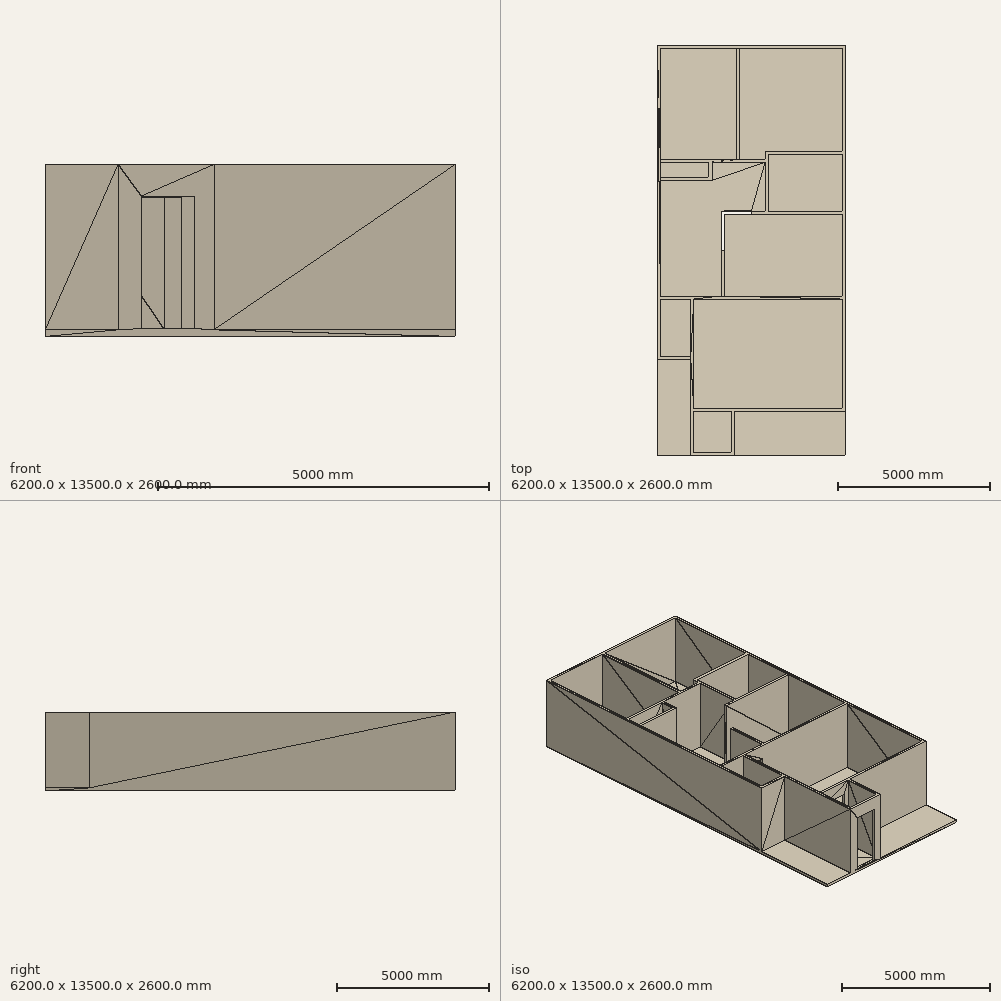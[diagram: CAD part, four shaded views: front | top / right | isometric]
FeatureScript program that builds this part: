
annotation { "Feature Type Name" : "Feature", "Feature Type Description" : "" }
export const myFeature = defineFeature(function(context is Context, id is Id, definition is map)
    precondition{}
    {
        {
            var Q0;
            Q0=qCreatedBy(makeId("Top.planeOp"),FACE);
            var sketch = newSketch(context, id + "F0", { "sketchPlane" : qUnion([Q0])});
            skLineSegment(sketch, "E0.bottom", {"start": v(-3100, -6750) * mm, "end": v(3100, -6750) * mm});
            skLineSegment(sketch, "E0.top", {"start": v(-3100, 6750) * mm, "end": v(3100, 6750) * mm});
            skLineSegment(sketch, "E0.left", {"start": v(-3100, -6750) * mm, "end": v(-3100, 6750) * mm});
            skLineSegment(sketch, "E0.right", {"start": v(3100, -6750) * mm, "end": v(3100, 6750) * mm});
            skPoint(sketch, "E0.middle", {"position": v(0, 0) * mm});
            skSolve(sketch);
        }
        {
            var Q0;
            Q0=qSketchRegion(id+"F0",true);
            extrude(context, id + "F1", {"entities" : qUnion([Q0]), "depth" : 100 * mm});
        }
        {
            var Q0;
            Q0=makeQuery(id+"F1.opExtrude","CAP_FACE",FACE,{"disambiguationData":[OSD([sQuery(id+"F0.wireOp",EDGE,"E0.bottom"),sQuery(id+"F0.wireOp",EDGE,"E0.top"),sQuery(id+"F0.wireOp",EDGE,"E0.left"),sQuery(id+"F0.wireOp",EDGE,"E0.right")])],"isStart":false});
            var sketch = newSketch(context, id + "F2", { "sketchPlane" : qUnion([Q0])});
            skLineSegment(sketch, "E1", {"start": v(-3100, 6750) * mm, "end": v(-3100, -3600) * mm});
            skLineSegment(sketch, "E2", {"start": v(-3100, -3600) * mm, "end": v(-2000, -3600) * mm});
            skLineSegment(sketch, "E3", {"start": v(-2000, -3600) * mm, "end": v(-2000, -6750) * mm});
            skLineSegment(sketch, "E4", {"start": v(-2000, -6750) * mm, "end": v(-550, -6750) * mm});
            skLineSegment(sketch, "E5", {"start": v(-550, -6750) * mm, "end": v(-550, -5300) * mm});
            skLineSegment(sketch, "E6", {"start": v(-550, -5300) * mm, "end": v(3100, -5300) * mm});
            skLineSegment(sketch, "E7", {"start": v(3100, -5300) * mm, "end": v(3100, 6750) * mm});
            skLineSegment(sketch, "E8", {"start": v(3100, 6750) * mm, "end": v(-3100, 6750) * mm});
            skLineSegment(sketch, "E9.0", {"start": v(3000, 6650) * mm, "end": v(-3000, 6650) * mm});
            skLineSegment(sketch, "E9.1", {"start": v(3000, -5200) * mm, "end": v(3000, 6650) * mm});
            skLineSegment(sketch, "E9.2", {"start": v(-3000, 6650) * mm, "end": v(-3000, -3500) * mm});
            skLineSegment(sketch, "E9.3", {"start": v(-650, -5200) * mm, "end": v(3000, -5200) * mm});
            skLineSegment(sketch, "E9.4", {"start": v(-3000, -3500) * mm, "end": v(-1900, -3500) * mm});
            skLineSegment(sketch, "E9.5", {"start": v(-1900, -3500) * mm, "end": v(-1900, -6650) * mm});
            skLineSegment(sketch, "E9.6", {"start": v(-1900, -6650) * mm, "end": v(-650, -6650) * mm});
            skLineSegment(sketch, "E9.7", {"start": v(-650, -6650) * mm, "end": v(-650, -5200) * mm});
            skSolve(sketch);
        }
        {
            var Q0;
            Q0=qSketchRegion(id+"F2",true);
            extrude(context, id + "F3", {"entities" : qUnion([Q0]), "operationType" : NewBodyOperationType.ADD, "depth" : 2500 * mm});
        }
        {
            var Q0;
            Q0=makeQuery(id+"F3.boolean.opBoolean","SPLIT",FACE,{"disambiguationData":[TD([makeQuery(id+"F3.opExtrude","SWEPT_FACE",FACE,{"disambiguationData":[OSD([sQuery(id+"F2.wireOp",EDGE,"E9.0")])]})])],"derivedFrom":makeQuery(id+"F1.opExtrude","CAP_FACE",FACE,{"disambiguationData":[OSD([sQuery(id+"F0.wireOp",EDGE,"E0.bottom"),sQuery(id+"F0.wireOp",EDGE,"E0.top"),sQuery(id+"F0.wireOp",EDGE,"E0.left"),sQuery(id+"F0.wireOp",EDGE,"E0.right")])],"isStart":false})});
            var sketch = newSketch(context, id + "F4", { "sketchPlane" : qUnion([Q0])});
            skLineSegment(sketch, "E10", {"start": v(-650, -5300) * mm, "end": v(-1900, -5300) * mm});
            skLineSegment(sketch, "E11", {"start": v(-1900, -5300) * mm, "end": v(-1900, -5200) * mm});
            skLineSegment(sketch, "E12", {"start": v(-1900, -5200) * mm, "end": v(-650, -5200) * mm});
            skLineSegment(sketch, "E13", {"start": v(-650, -5200) * mm, "end": v(-650, -5300) * mm});
            skSolve(sketch);
        }
        {
            var Q0;
            Q0=qSketchRegion(id+"F4",true);
            extrude(context, id + "F5", {"entities" : qUnion([Q0]), "operationType" : NewBodyOperationType.ADD, "depth" : 2500 * mm});
        }
        {
            var Q0;
            {var subQ3=makeQuery(id+"F3.opExtrude","SWEPT_FACE",FACE,{"disambiguationData":[OSD([sQuery(id+"F2.wireOp",EDGE,"E9.0")])]});Q0=makeQuery(id+"F5.boolean.opBoolean","SPLIT",FACE,{"disambiguationData":[TD([subQ3])],"derivedFrom":makeQuery(id+"F3.boolean.opBoolean","SPLIT",FACE,{"disambiguationData":[TD([subQ3])],"derivedFrom":makeQuery(id+"F1.opExtrude","CAP_FACE",FACE,{"disambiguationData":[OSD([sQuery(id+"F0.wireOp",EDGE,"E0.bottom"),sQuery(id+"F0.wireOp",EDGE,"E0.top"),sQuery(id+"F0.wireOp",EDGE,"E0.left"),sQuery(id+"F0.wireOp",EDGE,"E0.right")])],"isStart":false})})});}
            var sketch = newSketch(context, id + "F6", { "sketchPlane" : qUnion([Q0])});
            skLineSegment(sketch, "E14", {"start": v(-3000, -1600) * mm, "end": v(-3000, -1500) * mm});
            skLineSegment(sketch, "E15", {"start": v(-3000, -1500) * mm, "end": v(3000, -1500) * mm});
            skLineSegment(sketch, "E16", {"start": v(3000, -1500) * mm, "end": v(3000, -1600) * mm});
            skLineSegment(sketch, "E17", {"start": v(3000, -1600) * mm, "end": v(-3000, -1600) * mm});
            skSolve(sketch);
        }
        {
            var Q0;
            Q0=qSketchRegion(id+"F6",true);
            extrude(context, id + "F7", {"entities" : qUnion([Q0]), "operationType" : NewBodyOperationType.ADD, "depth" : 2500 * mm});
        }
        {
            var Q0;
            {var subQ1=makeQuery(id+"F3.opExtrude","SWEPT_FACE",FACE,{"disambiguationData":[OSD([sQuery(id+"F2.wireOp",EDGE,"E9.3")])]});var subQ6=makeQuery(id+"F3.opExtrude","SWEPT_FACE",FACE,{"disambiguationData":[OSD([sQuery(id+"F2.wireOp",EDGE,"E9.0")])]});Q0=makeQuery(id+"F7.boolean.opBoolean","SPLIT",FACE,{"disambiguationData":[TD([subQ1])],"derivedFrom":makeQuery(id+"F5.boolean.opBoolean","SPLIT",FACE,{"disambiguationData":[TD([subQ6])],"derivedFrom":makeQuery(id+"F3.boolean.opBoolean","SPLIT",FACE,{"disambiguationData":[TD([subQ6])],"derivedFrom":makeQuery(id+"F1.opExtrude","CAP_FACE",FACE,{"disambiguationData":[OSD([sQuery(id+"F0.wireOp",EDGE,"E0.bottom"),sQuery(id+"F0.wireOp",EDGE,"E0.top"),sQuery(id+"F0.wireOp",EDGE,"E0.left"),sQuery(id+"F0.wireOp",EDGE,"E0.right")])],"isStart":false})})})});}
            var sketch = newSketch(context, id + "F8", { "sketchPlane" : qUnion([Q0])});
            skLineSegment(sketch, "E18", {"start": v(-1900, -3500) * mm, "end": v(-1900, -1600) * mm});
            skLineSegment(sketch, "E19", {"start": v(-1900, -1600) * mm, "end": v(-2000, -1600) * mm});
            skLineSegment(sketch, "E20", {"start": v(-2000, -1600) * mm, "end": v(-2000, -3500) * mm});
            skLineSegment(sketch, "E21", {"start": v(-2000, -3500) * mm, "end": v(-1900, -3500) * mm});
            skSolve(sketch);
        }
        {
            var Q0;
            Q0=qSketchRegion(id+"F8",true);
            extrude(context, id + "F9", {"entities" : qUnion([Q0]), "operationType" : NewBodyOperationType.ADD, "depth" : 2500 * mm});
        }
        {
            var Q0;
            {var subQ0=makeQuery(id+"F3.opExtrude","SWEPT_FACE",FACE,{"disambiguationData":[OSD([sQuery(id+"F2.wireOp",EDGE,"E9.0")])]});Q0=makeQuery(id+"F7.boolean.opBoolean","SPLIT",FACE,{"disambiguationData":[TD([subQ0])],"derivedFrom":makeQuery(id+"F5.boolean.opBoolean","SPLIT",FACE,{"disambiguationData":[TD([subQ0])],"derivedFrom":makeQuery(id+"F3.boolean.opBoolean","SPLIT",FACE,{"disambiguationData":[TD([subQ0])],"derivedFrom":makeQuery(id+"F1.opExtrude","CAP_FACE",FACE,{"disambiguationData":[OSD([sQuery(id+"F0.wireOp",EDGE,"E0.bottom"),sQuery(id+"F0.wireOp",EDGE,"E0.top"),sQuery(id+"F0.wireOp",EDGE,"E0.left"),sQuery(id+"F0.wireOp",EDGE,"E0.right")])],"isStart":false})})})});}
            var sketch = newSketch(context, id + "F10", { "sketchPlane" : qUnion([Q0])});
            skLineSegment(sketch, "E22", {"start": v(-900, -1500) * mm, "end": v(-1000, -1500) * mm});
            skLineSegment(sketch, "E23", {"start": v(-1000, -1500) * mm, "end": v(-1000, 1300) * mm});
            skLineSegment(sketch, "E24", {"start": v(-1000, 1300) * mm, "end": v(450, 1300) * mm});
            skLineSegment(sketch, "E25", {"start": v(450, 1300) * mm, "end": v(450, 3250) * mm});
            skLineSegment(sketch, "E26", {"start": v(450, 3250) * mm, "end": v(3000, 3250) * mm});
            skLineSegment(sketch, "E27", {"start": v(3000, 3250) * mm, "end": v(3000, 3150) * mm});
            skLineSegment(sketch, "E28", {"start": v(3000, 3150) * mm, "end": v(550, 3150) * mm});
            skLineSegment(sketch, "E29", {"start": v(550, 3150) * mm, "end": v(550, 1300) * mm});
            skLineSegment(sketch, "E30", {"start": v(550, 1300) * mm, "end": v(3000, 1300) * mm});
            skLineSegment(sketch, "E31", {"start": v(3000, 1300) * mm, "end": v(3000, 1200) * mm});
            skLineSegment(sketch, "E32", {"start": v(3000, 1200) * mm, "end": v(-900, 1200) * mm});
            skLineSegment(sketch, "E33", {"start": v(-900, 1200) * mm, "end": v(-900, -1500) * mm});
            skSolve(sketch);
        }
        {
            var Q0;
            Q0=qSketchRegion(id+"F10",true);
            extrude(context, id + "F11", {"entities" : qUnion([Q0]), "operationType" : NewBodyOperationType.ADD, "depth" : 2500 * mm});
        }
        {
            var Q0;
            {var subQ3=makeQuery(id+"F3.opExtrude","SWEPT_FACE",FACE,{"disambiguationData":[OSD([sQuery(id+"F2.wireOp",EDGE,"E9.0")])]});Q0=makeQuery(id+"F11.boolean.opBoolean","SPLIT",FACE,{"disambiguationData":[TD([subQ3])],"derivedFrom":makeQuery(id+"F7.boolean.opBoolean","SPLIT",FACE,{"disambiguationData":[TD([subQ3])],"derivedFrom":makeQuery(id+"F5.boolean.opBoolean","SPLIT",FACE,{"disambiguationData":[TD([subQ3])],"derivedFrom":makeQuery(id+"F3.boolean.opBoolean","SPLIT",FACE,{"disambiguationData":[TD([subQ3])],"derivedFrom":makeQuery(id+"F1.opExtrude","CAP_FACE",FACE,{"disambiguationData":[OSD([sQuery(id+"F0.wireOp",EDGE,"E0.bottom"),sQuery(id+"F0.wireOp",EDGE,"E0.top"),sQuery(id+"F0.wireOp",EDGE,"E0.left"),sQuery(id+"F0.wireOp",EDGE,"E0.right")])],"isStart":false})})})})});}
            var sketch = newSketch(context, id + "F12", { "sketchPlane" : qUnion([Q0])});
            skLineSegment(sketch, "E34", {"start": v(450, 3000) * mm, "end": v(450, 2900) * mm});
            skLineSegment(sketch, "E35", {"start": v(450, 2900) * mm, "end": v(-1300, 2900) * mm});
            skLineSegment(sketch, "E36", {"start": v(-1300, 2900) * mm, "end": v(-1300, 2300) * mm});
            skLineSegment(sketch, "E37", {"start": v(-1300, 2300) * mm, "end": v(-3000, 2300) * mm});
            skLineSegment(sketch, "E38", {"start": v(-3000, 2300) * mm, "end": v(-3000, 2400) * mm});
            skLineSegment(sketch, "E39", {"start": v(-3000, 2400) * mm, "end": v(-1400, 2400) * mm});
            skLineSegment(sketch, "E40", {"start": v(-1400, 2400) * mm, "end": v(-1400, 2900) * mm});
            skLineSegment(sketch, "E41", {"start": v(-1400, 2900) * mm, "end": v(-3000, 2900) * mm});
            skLineSegment(sketch, "E42", {"start": v(-3000, 2900) * mm, "end": v(-3000, 3000) * mm});
            skLineSegment(sketch, "E43", {"start": v(-3000, 3000) * mm, "end": v(-500, 3000) * mm});
            skLineSegment(sketch, "E44", {"start": v(-500, 3000) * mm, "end": v(-500, 6650) * mm});
            skLineSegment(sketch, "E45", {"start": v(-500, 6650) * mm, "end": v(-400, 6650) * mm});
            skLineSegment(sketch, "E46", {"start": v(-400, 6650) * mm, "end": v(-400, 3000) * mm});
            skLineSegment(sketch, "E47", {"start": v(-400, 3000) * mm, "end": v(450, 3000) * mm});
            skSolve(sketch);
        }
        {
            var Q0;
            Q0=qSketchRegion(id+"F12",true);
            extrude(context, id + "F13", {"entities" : qUnion([Q0]), "operationType" : NewBodyOperationType.ADD, "depth" : 2500 * mm});
        }
        {
            var Q0;
            Q0=makeQuery(id+"F3.boolean.opBoolean","MERGE",FACE,{"derivedFrom":[makeQuery(id+"F1.opExtrude","SWEPT_FACE",FACE,{"disambiguationData":[OSD([sQuery(id+"F0.wireOp",EDGE,"E0.bottom")])]}),makeQuery(id+"F3.opExtrude","SWEPT_FACE",FACE,{"disambiguationData":[OSD([sQuery(id+"F2.wireOp",EDGE,"E4")])]})]});
            var sketch = newSketch(context, id + "F14", { "sketchPlane" : qUnion([Q0])});
            skLineSegment(sketch, "E48.bottom", {"start": v(-1650, 120) * mm, "end": v(-850, 120) * mm});
            skLineSegment(sketch, "E48.top", {"start": v(-1650, 2120) * mm, "end": v(-850, 2120) * mm});
            skLineSegment(sketch, "E48.left", {"start": v(-1650, 120) * mm, "end": v(-1650, 2120) * mm});
            skLineSegment(sketch, "E48.right", {"start": v(-850, 120) * mm, "end": v(-850, 2120) * mm});
            skSolve(sketch);
        }
        {
            var Q0;
            Q0=qSketchRegion(id+"F14",true);
            extrude(context, id + "F15", {"entities" : qUnion([Q0]), "operationType" : NewBodyOperationType.REMOVE, "endBound" : BoundingType.UP_TO_NEXT, "oppositeDirection" : true, "depth" : 25 * mm});
        }
        {
            var Q0;
            Q0=makeQuery(id+"F5.opExtrude","SWEPT_FACE",FACE,{"disambiguationData":[OSD([sQuery(id+"F4.wireOp",EDGE,"E10")])]});
            var sketch = newSketch(context, id + "F16", { "sketchPlane" : qUnion([Q0])});
            skLineSegment(sketch, "E49.bottom", {"start": v(-1650, 120) * mm, "end": v(-850, 120) * mm});
            skLineSegment(sketch, "E49.top", {"start": v(-1650, 2120) * mm, "end": v(-850, 2120) * mm});
            skLineSegment(sketch, "E49.left", {"start": v(-1650, 120) * mm, "end": v(-1650, 2120) * mm});
            skLineSegment(sketch, "E49.right", {"start": v(-850, 120) * mm, "end": v(-850, 2120) * mm});
            skSolve(sketch);
        }
        {
            var Q0;
            Q0=qSketchRegion(id+"F16",true);
            extrude(context, id + "F17", {"entities" : qUnion([Q0]), "operationType" : NewBodyOperationType.REMOVE, "endBound" : BoundingType.UP_TO_NEXT, "oppositeDirection" : true, "depth" : 25 * mm});
        }
        {
            var Q0;
            {var subQ2=sQuery(id+"F2.wireOp",EDGE,"E9.1");var subQ3=sQuery(id+"F6.wireOp",EDGE,"E17");Q0=makeQuery(id+"F9.boolean.opBoolean","SPLIT",FACE,{"disambiguationData":[TD([makeQuery(id+"F3.opExtrude","SWEPT_FACE",FACE,{"disambiguationData":[OSD([subQ2])]})])],"derivedFrom":makeQuery(id+"F7.opExtrude","SWEPT_FACE",FACE,{"disambiguationData":[OSD([subQ3])]})});}
            var sketch = newSketch(context, id + "F18", { "sketchPlane" : qUnion([Q0])});
            skLineSegment(sketch, "E50.bottom", {"start": v(-1850, 100) * mm, "end": v(-1050, 100) * mm});
            skLineSegment(sketch, "E50.top", {"start": v(-1850, 2100) * mm, "end": v(-1050, 2100) * mm});
            skLineSegment(sketch, "E50.left", {"start": v(-1850, 100) * mm, "end": v(-1850, 2100) * mm});
            skLineSegment(sketch, "E50.right", {"start": v(-1050, 100) * mm, "end": v(-1050, 2100) * mm});
            skSolve(sketch);
        }
        {
            var Q0;
            Q0=qSketchRegion(id+"F18",true);
            extrude(context, id + "F19", {"entities" : qUnion([Q0]), "operationType" : NewBodyOperationType.REMOVE, "endBound" : BoundingType.UP_TO_NEXT, "oppositeDirection" : true, "depth" : 25 * mm});
        }
        {
            var Q0;
            Q0=makeQuery(id+"F1.opExtrude","SWEPT_BODY",BODY,{"disambiguationData":[OSD([sQuery(id+"F0.wireOp",EDGE,"E0.bottom"),sQuery(id+"F0.wireOp",EDGE,"E0.top"),sQuery(id+"F0.wireOp",EDGE,"E0.left"),sQuery(id+"F0.wireOp",EDGE,"E0.right")])]});
            transform(context, id + "F20", {"entities" : qUnion([Q0]), "transformType" : TransformType.TRANSLATION_3D, "dx" : 0 * mm, "dy" : 0 * mm, "dz" : 0 * mm, "makeCopy" : true});
        }
        {
            var Q0;
            Q0=makeQuery(id+"F11.opExtrude","SWEPT_FACE",FACE,{"disambiguationData":[OSD([sQuery(id+"F10.wireOp",EDGE,"E32")])]});
            var sketch = newSketch(context, id + "F21", { "sketchPlane" : qUnion([Q0])});
            skLineSegment(sketch, "E51.bottom", {"start": v(-900, 2600) * mm, "end": v(0, 2600) * mm});
            skLineSegment(sketch, "E51.top", {"start": v(-900, 0) * mm, "end": v(0, 0) * mm});
            skLineSegment(sketch, "E51.left", {"start": v(-900, 2600) * mm, "end": v(-900, 0) * mm});
            skLineSegment(sketch, "E51.right", {"start": v(0, 2600) * mm, "end": v(0, 0) * mm});
            skSolve(sketch);
        }
        {
            var Q0;
            Q0 = qSketchRegion(id + "F21", true);
            extrude(context, id + "F22", {"entities" : qUnion([Q0]), "operationType" : NewBodyOperationType.REMOVE, "oppositeDirection" : true, "depth" : 101 * mm, "offsetDistance" : 25 * mm});
        }
        {
            var Q0;
            Q0=makeQuery(id+"F22.boolean.opBoolean","MERGE",FACE,{"derivedFrom":[makeQuery(id+"F11.opExtrude","SWEPT_FACE",FACE,{"disambiguationData":[OSD([sQuery(id+"F10.wireOp",EDGE,"E33")])]})],"fromTools":[makeQuery(id+"F22.opExtrude","SWEPT_FACE",FACE,{"disambiguationData":[OSD([sQuery(id+"F21.wireOp",EDGE,"E51.left")])]})]});
            var sketch = newSketch(context, id + "F23", { "sketchPlane" : qUnion([Q0])});
            skLineSegment(sketch, "E52.bottom", {"start": v(1300, 2600) * mm, "end": v(0, 2600) * mm});
            skLineSegment(sketch, "E52.top", {"start": v(1300, 0) * mm, "end": v(0, 0) * mm});
            skLineSegment(sketch, "E52.left", {"start": v(1300, 2600) * mm, "end": v(1300, 0) * mm});
            skLineSegment(sketch, "E52.right", {"start": v(0, 2600) * mm, "end": v(0, 0) * mm});
            skSolve(sketch);
        }
        {
            var Q0;
            Q0 = qSketchRegion(id + "F23", true);
            extrude(context, id + "F24", {"entities" : qUnion([Q0]), "operationType" : NewBodyOperationType.REMOVE, "oppositeDirection" : true, "depth" : 101 * mm, "offsetDistance" : 25 * mm});
        }
    });
